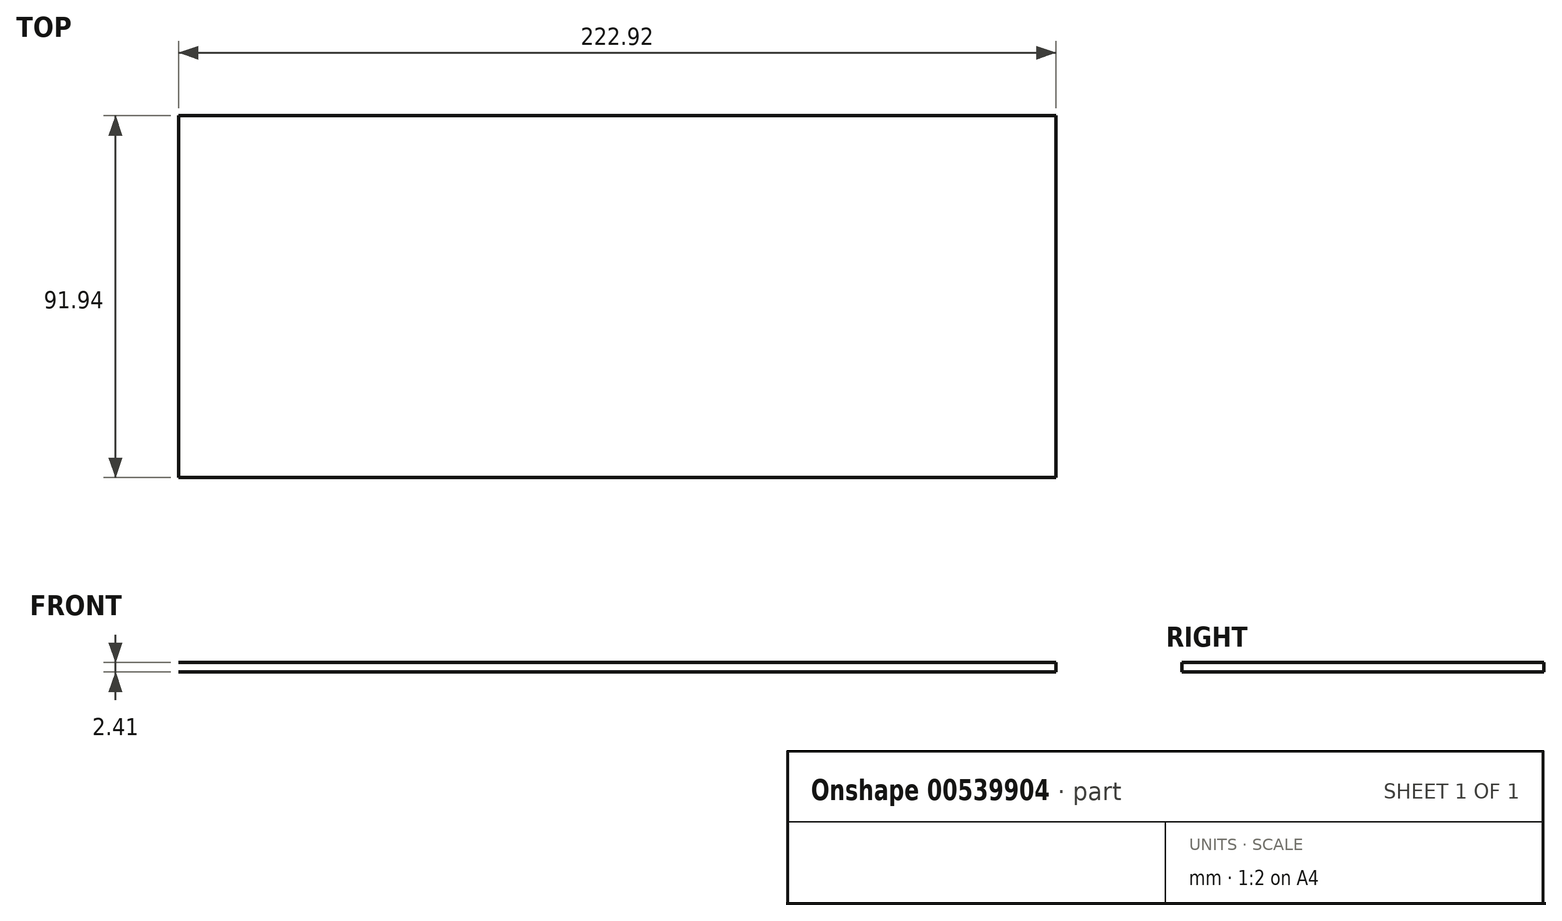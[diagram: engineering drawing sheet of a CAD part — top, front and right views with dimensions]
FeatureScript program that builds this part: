
annotation { "Feature Type Name" : "Feature", "Feature Type Description" : "" }
export const myFeature = defineFeature(function(context is Context, id is Id, definition is map)
    precondition{}
    {
        {
            var Q0;
            Q0=qCreatedBy(makeId("Front.planeOp"),FACE);
            var sketch = newSketch(context, id + "F0", { "sketchPlane" : qUnion([Q0])});
            skLineSegment(sketch, "E0.bottom", {"start": v(-139.63, 30.5) * mm, "end": v(83.3, 30.5) * mm});
            skLineSegment(sketch, "E0.top", {"start": v(-139.63, 28.1) * mm, "end": v(83.3, 28.1) * mm});
            skLineSegment(sketch, "E0.left", {"start": v(-139.63, 30.5) * mm, "end": v(-139.63, 28.1) * mm});
            skLineSegment(sketch, "E0.right", {"start": v(83.3, 30.5) * mm, "end": v(83.3, 28.1) * mm});
            skSolve(sketch);
        }
        {
            var Q0;
            Q0=sQuery(id+"F0.wireOp",EDGE,"E0.bottom");
            var Q1;
            Q1=sQuery(id+"F0.wireOp",EDGE,"E0.top");
            var Q2;
            Q2=sQuery(id+"F0.wireOp",EDGE,"E0.right");
            extrude(context, id + "F1", {"bodyType" : ToolBodyType.SURFACE, "surfaceEntities" : qUnion([Q0, Q1, Q2]), "endBound" : BoundingType.SYMMETRIC, "depth" : 91.95 * mm, "offsetDistance" : 25.4 * mm});
        }
    });
